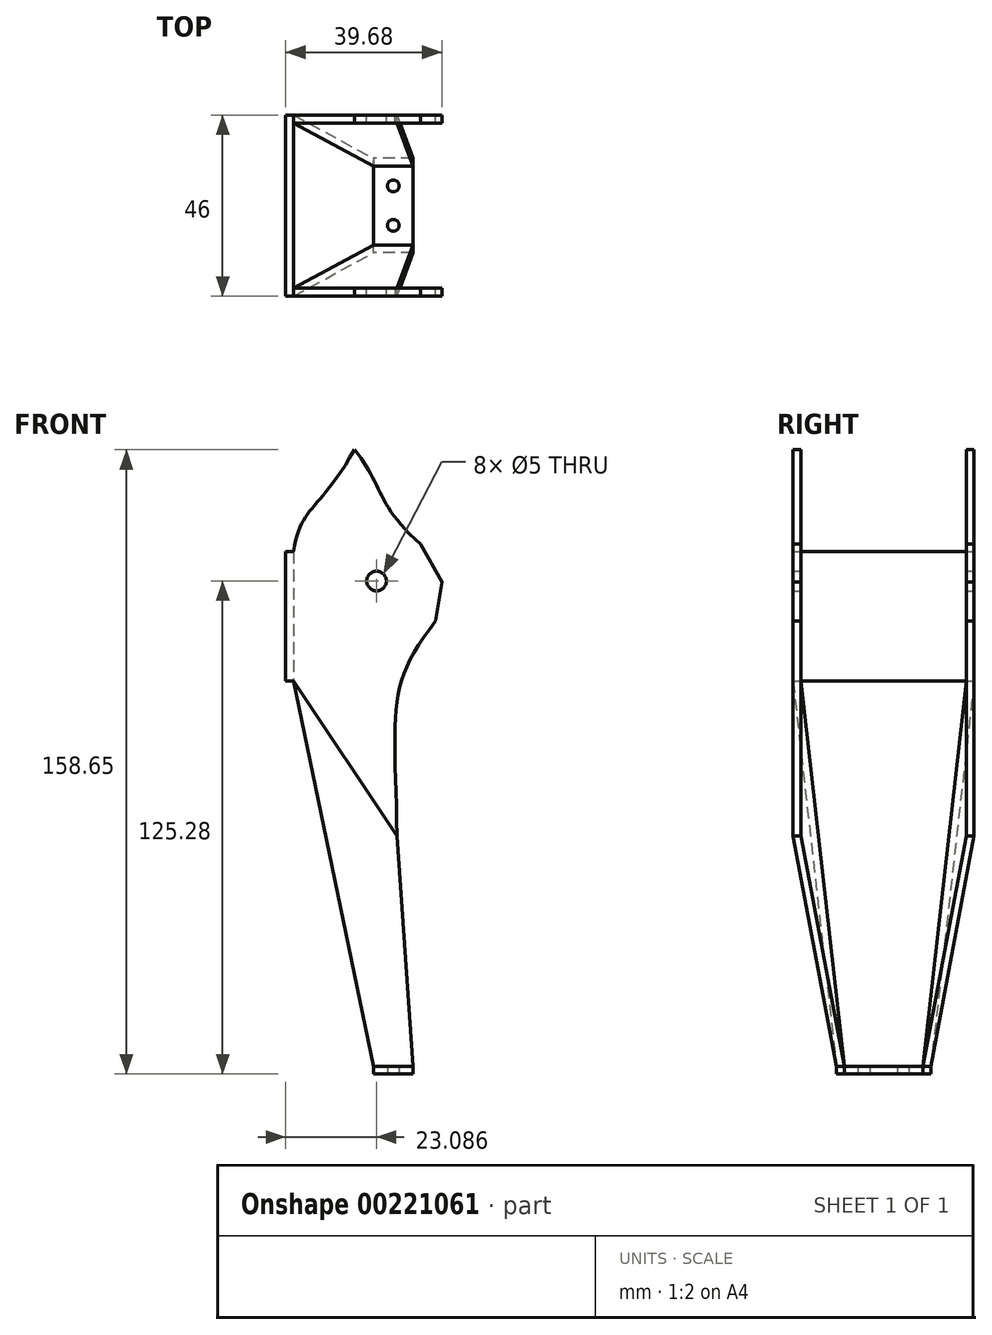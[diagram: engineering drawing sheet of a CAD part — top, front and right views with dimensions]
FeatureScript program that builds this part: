
annotation { "Feature Type Name" : "Feature", "Feature Type Description" : "" }
export const myFeature = defineFeature(function(context is Context, id is Id, definition is map)
    precondition{}
    {
        {
            var Q0;
            Q0=qCreatedBy(makeId("Front.planeOp"),FACE);
            var sketch = newSketch(context, id + "F0", { "sketchPlane" : qUnion([Q0])});
            skCircle(sketch, "E0", {"center": v(-36.31, 30.77) * mm, "radius": 2.5 * mm});
            skLineSegment(sketch, "E1", {"start": v(-57.44, 38.23) * mm, "end": v(-57.44, 5.36) * mm});
            skLineSegment(sketch, "E2", {"start": v(-25.18, 40.15) * mm, "end": v(-19.72, 30.45) * mm});
            skLineSegment(sketch, "E3", {"start": v(-57.44, 38.23) * mm, "end": v(-59.4, 38.23) * mm});
            skLineSegment(sketch, "E4", {"start": v(-59.4, 38.23) * mm, "end": v(-59.4, 5.36) * mm});
            skLineSegment(sketch, "E5", {"start": v(-59.4, 5.36) * mm, "end": v(-57.44, 5.36) * mm});
            skLineSegment(sketch, "E6", {"start": v(-19.72, 30.45) * mm, "end": v(-21.3, 20.58) * mm});
            skFitSpline(sketch, "E7", {"points": [v(-21.3, 20.58) * mm, v(-31.14, -35.38) * mm], "startDerivative": vector(-39.68, -51.32) * mm, "endDerivative": vector(1.08, -100.07) * mm});
            skLineSegment(sketch, "E8", {"start": v(-57.44, 5.36) * mm, "end": v(-31.15, -34.06) * mm});
            skFitSpline(sketch, "E9", {"points": [v(-41.94, 64.14) * mm, v(-25.18, 40.15) * mm], "startDerivative": vector(21.16, -25.4) * mm, "endDerivative": vector(34.39, -30.69) * mm});
            skFitSpline(sketch, "E10", {"points": [v(-41.94, 64.14) * mm, v(-57.44, 38.23) * mm], "startDerivative": vector(-28.04, -49.2) * mm, "endDerivative": vector(-6.11, -36.58) * mm});
            skLineSegment(sketch, "E11", {"start": v(-27.07, -94.51) * mm, "end": v(-37.07, -94.51) * mm});
            skLineSegment(sketch, "E12", {"start": v(-37.07, -94.51) * mm, "end": v(-37.07, -92.51) * mm});
            skLineSegment(sketch, "E13", {"start": v(-37.07, -92.51) * mm, "end": v(-27.07, -92.51) * mm});
            skLineSegment(sketch, "E14", {"start": v(-27.07, -92.51) * mm, "end": v(-27.07, -94.51) * mm});
            skSolve(sketch);
        }
        {
            var Q0;
            Q0=makeQuery(id+"F0.imprint","IMPRINT",FACE,{"disambiguationData":[TD([[makeQuery(id+"F0.imprint","IMPRINT",EDGE,{"derivedFrom":sQuery(id+"F0.wireOp",EDGE,"E0")}),-1.0]])]});
            var Q1;
            Q1=makeQuery(id+"F0.imprint","IMPRINT",FACE,{"disambiguationData":[TD([[makeQuery(id+"F0.imprint","IMPRINT",EDGE,{"derivedFrom":sQuery(id+"F0.wireOp",EDGE,"E1")}),-1.0]])]});
            extrude(context, id + "F1", {"entities" : qUnion([Q0, Q1]), "endBound" : BoundingType.SYMMETRIC, "depth" : 46 * mm});
        }
        {
            var Q0;
            Q0=makeQuery(id+"F0.imprint","IMPRINT",FACE,{"disambiguationData":[TD([[makeQuery(id+"F0.imprint","IMPRINT",EDGE,{"derivedFrom":sQuery(id+"F0.wireOp",EDGE,"E11")}),-1.0]])]});
            extrude(context, id + "F2", {"entities" : qUnion([Q0]), "depth" : 2 * mm});
        }
        {
            var Q0;
            Q0=makeQuery(id+"F0.imprint","IMPRINT",FACE,{"disambiguationData":[TD([[makeQuery(id+"F0.imprint","IMPRINT",EDGE,{"derivedFrom":sQuery(id+"F0.wireOp",EDGE,"E0")}),-1.0]])]});
            extrude(context, id + "F3", {"entities" : qUnion([Q0]), "operationType" : NewBodyOperationType.REMOVE, "endBound" : BoundingType.SYMMETRIC, "oppositeDirection" : true, "depth" : 42 * mm});
        }
        {
            var Q0;
            Q0=makeQuery(id+"F2.opExtrude","SWEPT_BODY",BODY,{"disambiguationData":[OSD([sQuery(id+"F0.wireOp",EDGE,"E11"),sQuery(id+"F0.wireOp",EDGE,"E12"),sQuery(id+"F0.wireOp",EDGE,"E13"),sQuery(id+"F0.wireOp",EDGE,"E14")])]});
            transform(context, id + "F4", {"entities" : qUnion([Q0]), "transformType" : TransformType.TRANSLATION_3D, "dx" : 0 * mm, "dy" : -10 * mm, "dz" : 0 * mm, "makeCopy" : false});
        }
        {
            var Q0;
            Q0=makeQuery(id+"F0.imprint","IMPRINT",FACE,{"disambiguationData":[TD([[makeQuery(id+"F0.imprint","IMPRINT",EDGE,{"derivedFrom":sQuery(id+"F0.wireOp",EDGE,"E11")}),-1.0]])]});
            extrude(context, id + "F5", {"entities" : qUnion([Q0]), "oppositeDirection" : true, "depth" : 2 * mm});
        }
        {
            var Q0;
            Q0=makeQuery(id+"F5.opExtrude","SWEPT_BODY",BODY,{"disambiguationData":[OSD([sQuery(id+"F0.wireOp",EDGE,"E11"),sQuery(id+"F0.wireOp",EDGE,"E12"),sQuery(id+"F0.wireOp",EDGE,"E13"),sQuery(id+"F0.wireOp",EDGE,"E14")])]});
            transform(context, id + "F6", {"entities" : qUnion([Q0]), "transformType" : TransformType.TRANSLATION_3D, "dx" : 0 * mm, "dy" : 10 * mm, "dz" : 0 * mm, "makeCopy" : false});
        }
        {
            var Q0;
            {var subQ0=sQuery(id+"F0.wireOp",EDGE,"E10");var subQ1=sQuery(id+"F0.wireOp",EDGE,"E9");var subQ2=sQuery(id+"F0.wireOp",EDGE,"E8");var subQ3=sQuery(id+"F0.wireOp",EDGE,"E7");var subQ4=sQuery(id+"F0.wireOp",EDGE,"E6");var subQ5=sQuery(id+"F0.wireOp",EDGE,"E2");var subQ6=sQuery(id+"F0.wireOp",EDGE,"E1");var subQ7=sQuery(id+"F0.wireOp",EDGE,"E0");Q0=makeQuery(id+"F3.boolean.opBoolean","SPLIT",FACE,{"disambiguationData":[TD([makeQuery(id+"F3.opExtrude","CAP_FACE",FACE,{"disambiguationData":[OSD([subQ7,subQ6,subQ5,subQ4,subQ3,subQ2,subQ1,subQ0])],"isStart":true})])],"derivedFrom":makeQuery(id+"F1.opExtrude","SWEPT_FACE",FACE,{"disambiguationData":[OSD([subQ2])]})});}
            var Q1;
            Q1=makeQuery(id+"F2.opExtrude","SWEPT_FACE",FACE,{"disambiguationData":[OSD([sQuery(id+"F0.wireOp",EDGE,"E13")])]});
            loft(context, id + "F7", {"sheetProfilesArray" : [{ "sheetProfileEntities" : qUnion([Q0]) }, { "sheetProfileEntities" : qUnion([Q1]) }]});
        }
        {
            var Q0;
            {var subQ0=sQuery(id+"F0.wireOp",EDGE,"E10");var subQ1=sQuery(id+"F0.wireOp",EDGE,"E9");var subQ2=sQuery(id+"F0.wireOp",EDGE,"E8");var subQ3=sQuery(id+"F0.wireOp",EDGE,"E7");var subQ4=sQuery(id+"F0.wireOp",EDGE,"E6");var subQ5=sQuery(id+"F0.wireOp",EDGE,"E2");var subQ6=sQuery(id+"F0.wireOp",EDGE,"E1");var subQ7=sQuery(id+"F0.wireOp",EDGE,"E0");Q0=makeQuery(id+"F3.boolean.opBoolean","SPLIT",FACE,{"disambiguationData":[TD([makeQuery(id+"F3.opExtrude","CAP_FACE",FACE,{"disambiguationData":[OSD([subQ7,subQ6,subQ5,subQ4,subQ3,subQ2,subQ1,subQ0])],"isStart":false})])],"derivedFrom":makeQuery(id+"F1.opExtrude","SWEPT_FACE",FACE,{"disambiguationData":[OSD([subQ2])]})});}
            var Q1;
            Q1=makeQuery(id+"F5.opExtrude","SWEPT_FACE",FACE,{"disambiguationData":[OSD([sQuery(id+"F0.wireOp",EDGE,"E13")])]});
            loft(context, id + "F8", {"sheetProfilesArray" : [{ "sheetProfileEntities" : qUnion([Q0]) }, { "sheetProfileEntities" : qUnion([Q1]) }]});
        }
        {
            var Q0;
            Q0=makeQuery(id+"F2.opExtrude","SWEPT_FACE",FACE,{"disambiguationData":[OSD([sQuery(id+"F0.wireOp",EDGE,"E11")])]});
            var sketch = newSketch(context, id + "F9", { "sketchPlane" : qUnion([Q0])});
            skLineSegment(sketch, "E15.bottom", {"start": v(-37.07, 12) * mm, "end": v(-27.07, 12) * mm});
            skLineSegment(sketch, "E15.top", {"start": v(-37.07, -12) * mm, "end": v(-27.07, -12) * mm});
            skLineSegment(sketch, "E15.left", {"start": v(-37.07, 12) * mm, "end": v(-37.07, -12) * mm});
            skLineSegment(sketch, "E15.right", {"start": v(-27.07, 12) * mm, "end": v(-27.07, -12) * mm});
            skCircle(sketch, "E16", {"center": v(-32.07, 5) * mm, "radius": 1.5 * mm});
            skCircle(sketch, "E17", {"center": v(-32.07, -5) * mm, "radius": 1.5 * mm});
            skSolve(sketch);
        }
        {
            var Q0;
            {var subQ2=sQuery(id+"F9.wireOp",EDGE,"E15.top");Q0=makeQuery(id+"F9.imprint","IMPRINT",FACE,{"disambiguationData":[TD([[makeQuery(id+"F9.imprint","IMPRINT",EDGE,{"derivedFrom":subQ2}),1.0]])]});}
            extrude(context, id + "F10", {"entities" : qUnion([Q0]), "oppositeDirection" : true, "depth" : 2 * mm});
        }
    });
